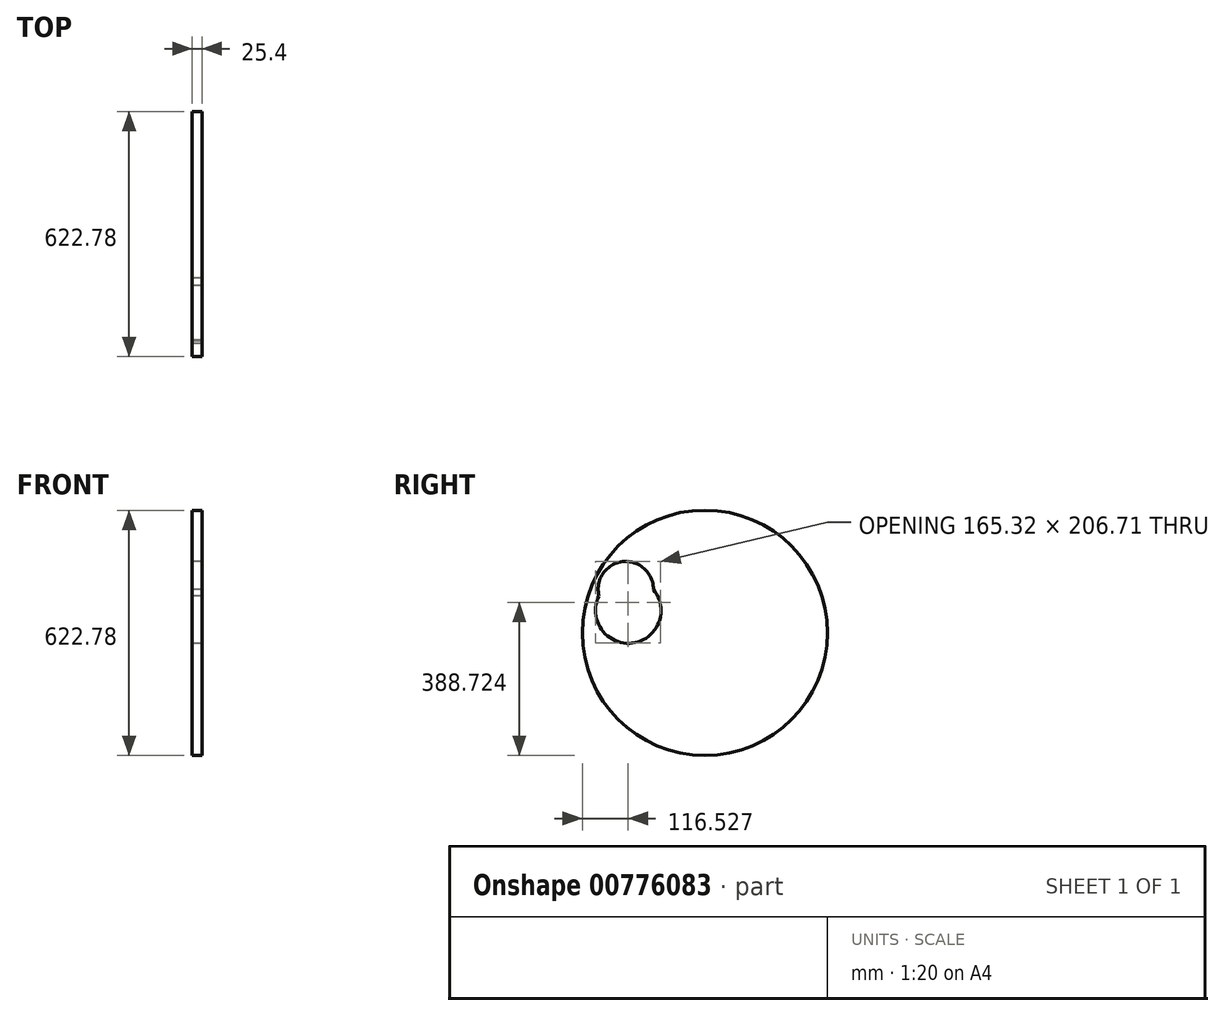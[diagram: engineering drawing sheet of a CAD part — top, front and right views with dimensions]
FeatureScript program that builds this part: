
annotation { "Feature Type Name" : "Feature", "Feature Type Description" : "" }
export const myFeature = defineFeature(function(context is Context, id is Id, definition is map)
    precondition{}
    {
        {
            var Q0;
            Q0=qCreatedBy(makeId("Right.planeOp"),FACE);
            var sketch = newSketch(context, id + "F0", { "sketchPlane" : qUnion([Q0])});
            skCircle(sketch, "E0", {"center": v(-170.12, 20.68) * mm, "radius": 83.33 * mm});
            skCircle(sketch, "E1", {"center": v(-176.64, 74.96) * mm, "radius": 70.2 * mm});
            skCircle(sketch, "E2", {"center": v(24.31, -36.04) * mm, "radius": 311.39 * mm});
            skSolve(sketch);
        }
        {
            var Q0;
            Q0 = qSketchRegion(id + "F0", true);
            extrude(context, id + "F1", {"entities" : qUnion([Q0]), "depth" : 25.4 * mm, "offsetDistance" : 25.4 * mm});
        }
    });
